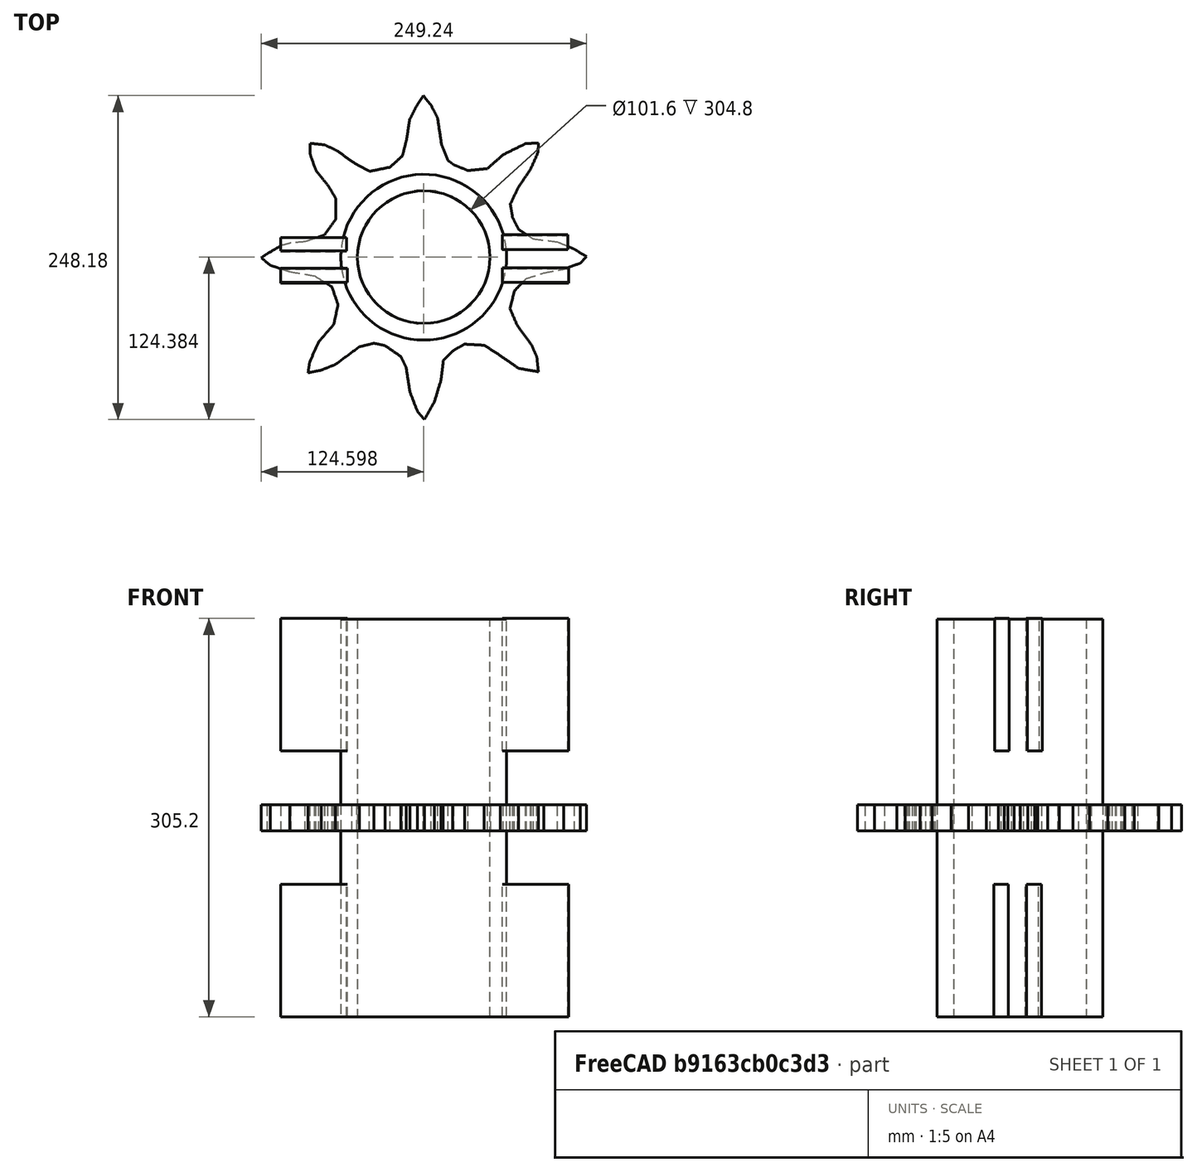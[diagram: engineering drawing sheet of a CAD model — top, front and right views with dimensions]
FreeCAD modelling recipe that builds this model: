
FCSTD DOCUMENT  (FreeCAD 0.16R6668 (Git))
Label: sprocket
License: All rights reserved
LicenseURL: http://en.wikipedia.org/wiki/All_rights_reserved
objects: Part::Feature×2, Part::FeaturePython×1, Sketcher::SketchObject×1, PartDesign::Pad×1
note: 6 computed .brp shape members not serialized (recipe doc carries the construction recipe); baked Part::Feature solids carry a one-line shape summary decoded from their .brp

FEATURE [Part::FeaturePython] Scale  # WARN: FeaturePython — macro-defined, semantics opaque (R4)
  Placement = pos=(-9.06814,-3.77073,-10.0508) rot=(0,0,1;0rad)
  Scale = (25.4,25.4,2)
FEATURE [Sketcher::SketchObject] Sketch
  sketch-geometry (2):
    g0: Circle CenterX=-9.09223 CenterY=-3.89611 CenterZ=0 NormalX=0 NormalY=0 NormalZ=1 Radius=50.8
    g1: Circle CenterX=-9.09223 CenterY=-3.89611 CenterZ=0 NormalX=0 NormalY=0 NormalZ=1 Radius=63.5
  constraints (2):
    c: Radius(g0) = 50.8
    c: Radius(g1) = 63.5
FEATURE [PartDesign::Pad] Pad001
  Length = 304.8
  Length2 = 100
  Midplane = true
  Sketch = -> Sketch
  Type = 0
FEATURE [Part::Feature] Pad004
  Placement = pos=(0,-5.14213,-152.4) rot=(0,0,1;0rad)
  shape: bbox 220.8 x 36.67 x 101.6 mm, 24 faces, 4 solids (baked)
FEATURE [Part::Feature] Pad003
  Placement = pos=(0,-4.48794,51.202) rot=(0,0,1;0rad)
  shape: bbox 220.8 x 36.67 x 101.6 mm, 24 faces, 4 solids (baked)
